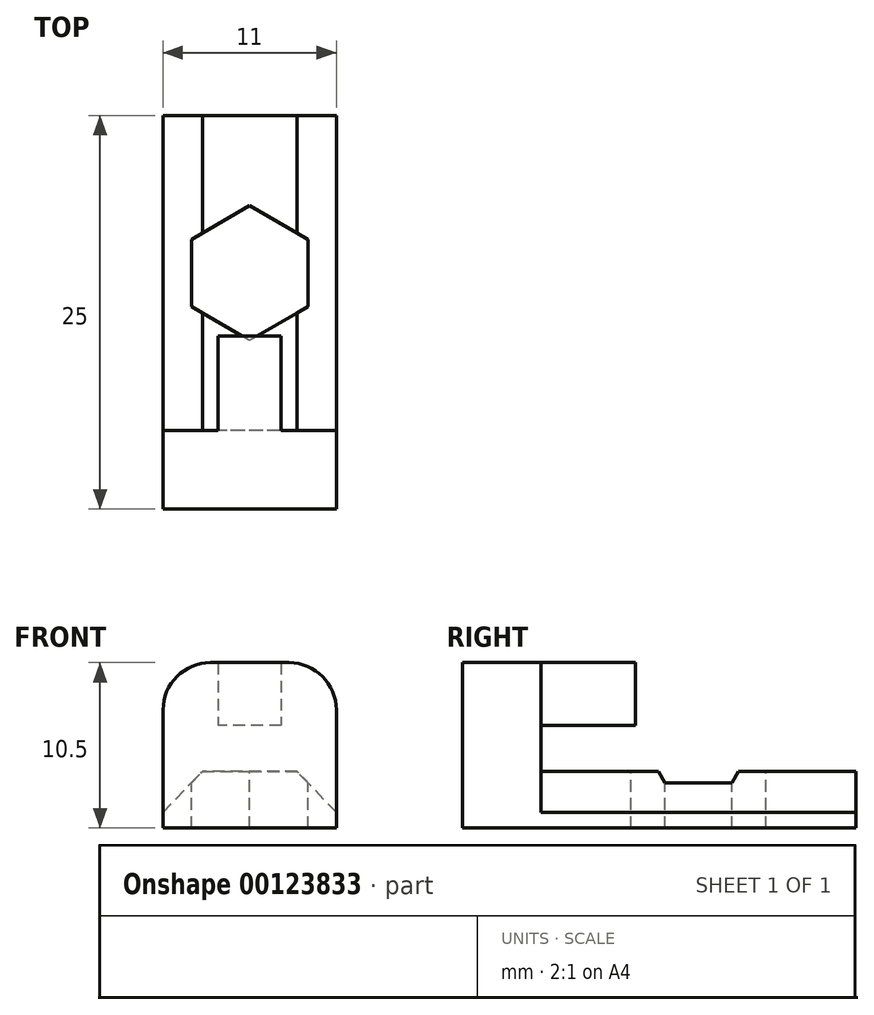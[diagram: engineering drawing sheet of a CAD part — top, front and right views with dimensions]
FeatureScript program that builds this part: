
annotation { "Feature Type Name" : "Feature", "Feature Type Description" : "" }
export const myFeature = defineFeature(function(context is Context, id is Id, definition is map)
    precondition{}
    {
        {
            var Q0;
            Q0=qCreatedBy(makeId("Front.planeOp"),FACE);
            var sketch = newSketch(context, id + "F0", { "sketchPlane" : qUnion([Q0])});
            skLineSegment(sketch, "E0", {"start": v(5.5, 0) * mm, "end": v(5.5, 1) * mm});
            skLineSegment(sketch, "E1", {"start": v(5.5, 1) * mm, "end": v(3, 3.6) * mm});
            skLineSegment(sketch, "E2", {"start": v(3, 3.6) * mm, "end": v(0, 3.6) * mm});
            skLineSegment(sketch, "E3", {"start": v(0, 0) * mm, "end": v(0, 3.6) * mm, "construction": true});
            skLineSegment(sketch, "E4.MirrorCS", {"start": v(-3, 3.6) * mm, "end": v(0, 3.6) * mm});
            skLineSegment(sketch, "E5.MirrorCS", {"start": v(-5.5, 1) * mm, "end": v(-3, 3.6) * mm});
            skLineSegment(sketch, "E6.MirrorCS", {"start": v(-5.5, 0) * mm, "end": v(-5.5, 1) * mm});
            skLineSegment(sketch, "E7", {"start": v(5.5, 0) * mm, "end": v(-5.5, 0) * mm});
            skSolve(sketch);
        }
        {
            var Q0;
            Q0=makeQuery(id+"F0.imprint","IMPRINT",FACE,{"disambiguationData":[TD([[makeQuery(id+"F0.imprint","IMPRINT",EDGE,{"derivedFrom":sQuery(id+"F0.wireOp",EDGE,"E0")}),1.0]])]});
            extrude(context, id + "F1", {"entities" : qUnion([Q0]), "depth" : 20 * mm});
        }
        {
            var Q0;
            Q0=makeQuery(id+"F1.opExtrude","SWEPT_FACE",FACE,{"disambiguationData":[OSD([sQuery(id+"F0.wireOp",EDGE,"E2"),sQuery(id+"F0.wireOp",EDGE,"E4.MirrorCS")])]});
            var sketch = newSketch(context, id + "F2", { "sketchPlane" : qUnion([Q0])});
            skLineSegment(sketch, "E8", {"start": v(-3, -10) * mm, "end": v(3.7, -10) * mm, "construction": true});
            skLineSegment(sketch, "E9", {"start": v(0, 0) * mm, "end": v(0, -20) * mm, "construction": true});
            skLineSegment(sketch, "E10", {"start": v(0, -5.73) * mm, "end": v(-3.7, -7.86) * mm});
            skLineSegment(sketch, "E11", {"start": v(-3.7, -7.86) * mm, "end": v(-3.7, -12.14) * mm});
            skLineSegment(sketch, "E12", {"start": v(-3.7, -12.14) * mm, "end": v(0, -14.27) * mm});
            skLineSegment(sketch, "E13", {"start": v(0, -14.27) * mm, "end": v(3.7, -12.14) * mm});
            skLineSegment(sketch, "E14", {"start": v(3.7, -12.14) * mm, "end": v(3.7, -7.86) * mm});
            skLineSegment(sketch, "E15", {"start": v(3.7, -7.86) * mm, "end": v(0, -5.73) * mm});
            skSolve(sketch);
        }
        {
            var Q0;
            {var subQ7=sQuery(id+"F2.wireOp",EDGE,"E15");var subQ8=sQuery(id+"F2.wireOp",EDGE,"E10");var subQ9=makeQuery(id+"F2.imprint","INTERSECT",VERTEX,{"derivedFrom":[subQ8,subQ7]});Q0=makeQuery(id+"F2.imprint","IMPRINT",FACE,{"disambiguationData":[TD([[makeQuery(id+"F2.imprint","IMPRINT",EDGE,{"disambiguationData":[TD([[subQ9,-1.0]])],"derivedFrom":subQ8}),1.0]])]});}
            var Q1;
            {var subQ0=sQuery(id+"F2.wireOp",EDGE,"E14");Q1=makeQuery(id+"F2.imprint","IMPRINT",FACE,{"disambiguationData":[TD([[makeQuery(id+"F2.imprint","IMPRINT",EDGE,{"derivedFrom":subQ0}),1.0]])]});}
            var Q2;
            {var subQ0=sQuery(id+"F2.wireOp",EDGE,"E11");Q2=makeQuery(id+"F2.imprint","IMPRINT",FACE,{"disambiguationData":[TD([[makeQuery(id+"F2.imprint","IMPRINT",EDGE,{"derivedFrom":subQ0}),1.0]])]});}
            var Q3;
            Q3=makeQuery(id+"F1.opExtrude","SWEPT_FACE",FACE,{"disambiguationData":[OSD([sQuery(id+"F0.wireOp",EDGE,"E7")])]});
            extrude(context, id + "F3", {"entities" : qUnion([Q0, Q1, Q2]), "operationType" : NewBodyOperationType.REMOVE, "endBound" : BoundingType.UP_TO_SURFACE, "oppositeDirection" : true, "endBoundEntityFace" : qUnion([Q3]), "depth" : 3.5 * mm});
        }
        {
            var Q0;
            Q0=makeQuery(id+"F1.opExtrude","SWEPT_FACE",FACE,{"disambiguationData":[OSD([sQuery(id+"F0.wireOp",EDGE,"E7")])]});
            var sketch = newSketch(context, id + "F4", { "sketchPlane" : qUnion([Q0])});
            skLineSegment(sketch, "E16.bottom", {"start": v(-5.5, 20) * mm, "end": v(5.5, 20) * mm});
            skLineSegment(sketch, "E16.top", {"start": v(-5.5, 25) * mm, "end": v(5.5, 25) * mm});
            skLineSegment(sketch, "E16.left", {"start": v(-5.5, 20) * mm, "end": v(-5.5, 25) * mm});
            skLineSegment(sketch, "E16.right", {"start": v(5.5, 20) * mm, "end": v(5.5, 25) * mm});
            skSolve(sketch);
        }
        {
            var Q0;
            Q0=makeQuery(id+"F4.imprint","IMPRINT",FACE,{"disambiguationData":[TD([[makeQuery(id+"F4.imprint","IMPRINT",EDGE,{"derivedFrom":sQuery(id+"F4.wireOp",EDGE,"E16.bottom")}),-1.0]])]});
            extrude(context, id + "F5", {"entities" : qUnion([Q0]), "operationType" : NewBodyOperationType.ADD, "oppositeDirection" : true, "depth" : 10.5 * mm});
        }
        {
            var Q0;
            Q0=makeQuery(id+"F5.opExtrude","SWEPT_FACE",FACE,{"disambiguationData":[OSD([sQuery(id+"F4.wireOp",EDGE,"E16.bottom")])]});
            var sketch = newSketch(context, id + "F6", { "sketchPlane" : qUnion([Q0])});
            skLineSegment(sketch, "E17.bottom", {"start": v(-2, 10.5) * mm, "end": v(2, 10.5) * mm});
            skLineSegment(sketch, "E17.top", {"start": v(-2, 6.5) * mm, "end": v(2, 6.5) * mm});
            skLineSegment(sketch, "E17.left", {"start": v(-2, 10.5) * mm, "end": v(-2, 6.5) * mm});
            skLineSegment(sketch, "E17.right", {"start": v(2, 10.5) * mm, "end": v(2, 6.5) * mm});
            skPoint(sketch, "E17.middle", {"position": v(0, 8.5) * mm});
            skSolve(sketch);
        }
        {
            var Q0;
            Q0=makeQuery(id+"F6.imprint","IMPRINT",FACE,{"disambiguationData":[TD([[makeQuery(id+"F6.imprint","IMPRINT",EDGE,{"derivedFrom":sQuery(id+"F6.wireOp",EDGE,"E17.bottom")}),-1.0]])]});
            extrude(context, id + "F7", {"entities" : qUnion([Q0]), "operationType" : NewBodyOperationType.ADD, "depth" : 6 * mm});
        }
        {
            var Q0;
            Q0=makeQuery(id+"F5.opExtrude","CAP_EDGE",EDGE,{"disambiguationData":[OSD([sQuery(id+"F4.wireOp",EDGE,"E16.left")])],"isStart":false});
            var Q1;
            Q1=makeQuery(id+"F5.opExtrude","CAP_EDGE",EDGE,{"disambiguationData":[OSD([sQuery(id+"F4.wireOp",EDGE,"E16.right")])],"isStart":false});
            fillet(context, id + "F8", {"entities" : qUnion([Q0, Q1]), "radius" : 3 * mm, "tangentPropagation" : true, "allowEdgeOverflow" : false});
        }
    });
